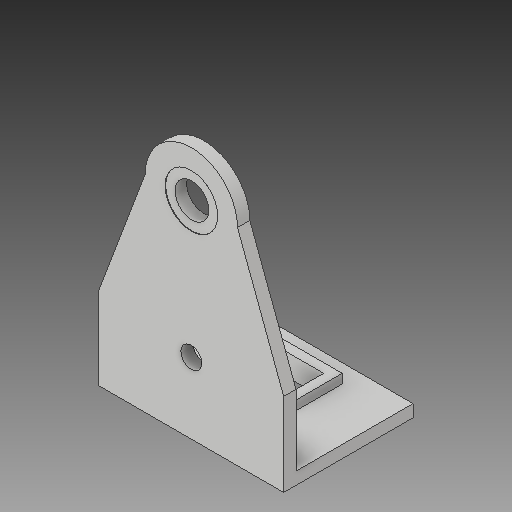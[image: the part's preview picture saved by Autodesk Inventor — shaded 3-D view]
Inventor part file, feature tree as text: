
AUTODESK INVENTOR PART (.ipt)
format: ipt  version: 2019 (Build 230136000, 136)  size: 166,400 bytes
history: native  units: mm
features: extrude x6, sketch x6, projected_geometry x1
ambient origin geometry x8: Origin, YZ Plane, XZ Plane, XY Plane, X Axis, Y Axis, Z Axis, Center Point
bodies: Body1 (feature_tree)
feature tree (13):
  extrude  "Extrusion1"  Depth=10.0mm
  extrude  "Extrusion2"  Depth=5.5mm
  extrude  "Extrusion3"  Depth=30.0mm
  extrude  "Extrusion4"  Depth=3.4mm
  extrude  "Extrusion5"  Depth=3.5mm TaperAngle=0.0deg
  extrude  "Extrusion6"  Depth=19.0mm TaperAngle=0.0deg
  sketch  "Sketch2"  dims[d15=30.0mm d16=10.0mm]
  sketch  "Sketch3"  dims[d17=15.0mm d18=5.5mm]
  projected_geometry  "Projected Loop1"
  sketch  "Sketch4"  dims[d19=30.0mm d20=8.0mm]
  sketch  "Sketch5"  dims[d21=15.0mm d22=3.4mm]
  sketch  "Sketch6"  dims[d23=2.0mm d24=0.0mm d25=3.5mm d26=0.0mm]
  sketch  "Sketch7"  dims[d27=2.0mm d28=19.0mm d29=0.0mm d31=10.0mm d32=9.5mm d33=10.0mm d34=10.0mm d35=0.0mm d36=1.5mm d37=1.5mm d38=0.0mm d39=8.55mm d40=0.1mm d41=0.0mm]
